FCSTD DOCUMENT  (FreeCAD 0.19R0.19.2)
Label: laptopStand010
License: All rights reserved
LicenseURL: http://en.wikipedia.org/wiki/All_rights_reserved
objects: Sketcher::SketchObject×1
note: 1 computed .brp shape members not serialized (recipe doc carries the construction recipe); baked Part::Feature solids carry a one-line shape summary decoded from their .brp

FEATURE [Sketcher::SketchObject] Sketch
  FullyConstrained = true
  sketch-geometry (10):
    g0: LineSegment StartX=-22.9272 StartY=136.221 StartZ=0 EndX=-22.9272 EndY=-103.779 EndZ=0
    g1: LineSegment StartX=-22.9272 StartY=136.221 StartZ=0 EndX=387.073 EndY=136.221 EndZ=0
    g2: LineSegment StartX=-22.9272 StartY=-103.779 StartZ=0 EndX=387.073 EndY=-103.779 EndZ=0
    g3: LineSegment StartX=387.073 StartY=136.221 StartZ=0 EndX=387.073 EndY=-103.779 EndZ=0
    g4: LineSegment StartX=387.073 StartY=136.221 StartZ=0 EndX=387.073 EndY=124.221 EndZ=0
    g5: LineSegment StartX=387.073 StartY=124.221 StartZ=0 EndX=375.073 EndY=124.221 EndZ=0
    g6: LineSegment StartX=-22.9272 StartY=-103.779 StartZ=0 EndX=-34.9272 EndY=-103.779 EndZ=0
    g7: LineSegment StartX=-34.9272 StartY=-103.779 StartZ=0 EndX=-34.9272 EndY=-91.7794 EndZ=0
    g8: LineSegment StartX=-34.9272 StartY=-91.7794 StartZ=0 EndX=375.073 EndY=124.221 EndZ=0
    g9: LineSegment StartX=-22.9272 StartY=136.221 StartZ=0 EndX=-10.9272 EndY=136.221 EndZ=0
  constraints (28):
    c: Vertical(g0)
    c: Distance(g0) = 240
    c: Horizontal(g1)
    c: Distance(g1) = 410
    c: Coincident(g1,g0)
    c: Coincident(g2,g0)
    c: Horizontal(g2)
    c: Coincident(g3,g1)
    c: Vertical(g3)
    c: Coincident(g2,g3)
    c: Block(g1)
    c: Vertical(g4)
    c: Distance(g4) = 12
    c: Coincident(g4,g1)
    c: Coincident(g5,g4)
    c: Horizontal(g5)
    c: Distance(g5) = 12
    c: Horizontal(g6)
    c: Distance(g6) = 12
    c: Coincident(g6,g0)
    c: Coincident(g7,g6)
    c: Vertical(g7)
    c: Distance(g7) = 12
    c: Coincident(g8,g7)
    c: Coincident(g8,g5)
    c: Horizontal(g9)
    c: Distance(g9) = 12
    c: Coincident(g0,g9)
